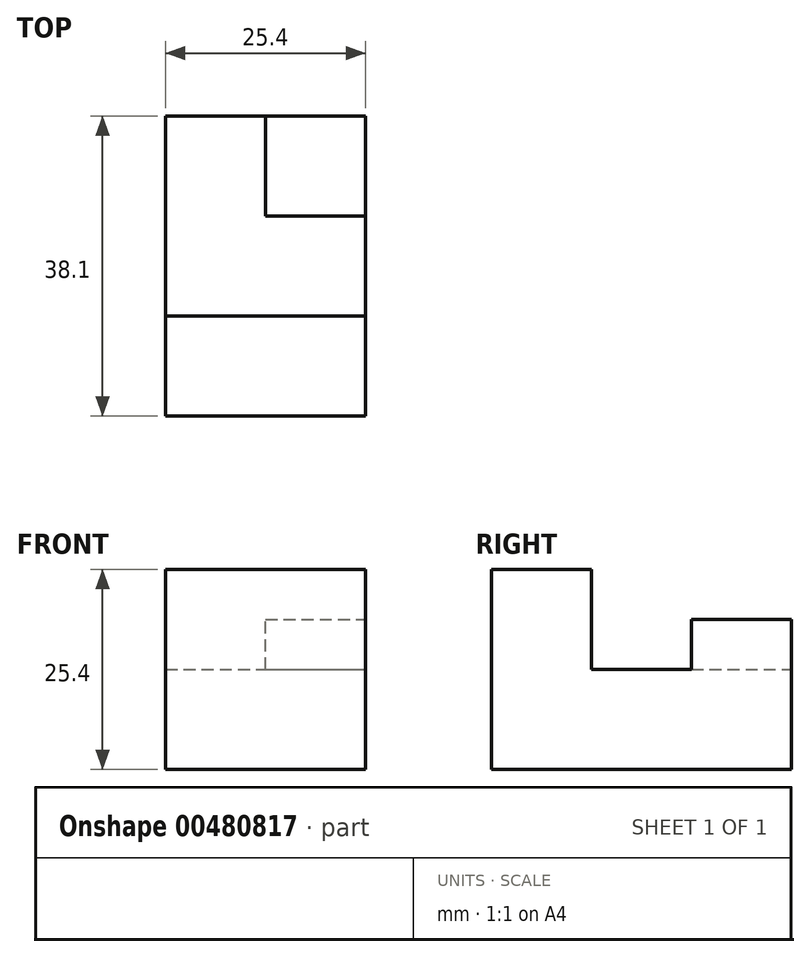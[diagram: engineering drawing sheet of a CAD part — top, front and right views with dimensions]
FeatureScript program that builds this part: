
annotation { "Feature Type Name" : "Feature", "Feature Type Description" : "" }
export const myFeature = defineFeature(function(context is Context, id is Id, definition is map)
    precondition{}
    {
        {
            var Q0;
            Q0=qCreatedBy(makeId("Right.planeOp"),FACE);
            var sketch = newSketch(context, id + "F0", { "sketchPlane" : qUnion([Q0])});
            skLineSegment(sketch, "E0", {"start": v(-38.1, 25.4) * mm, "end": v(-38.1, 0) * mm});
            skLineSegment(sketch, "E1", {"start": v(-38.1, 0) * mm, "end": v(0, 0) * mm});
            skLineSegment(sketch, "E2", {"start": v(0, 0) * mm, "end": v(0, 12.7) * mm});
            skLineSegment(sketch, "E3", {"start": v(0, 12.7) * mm, "end": v(-25.4, 12.7) * mm});
            skLineSegment(sketch, "E4", {"start": v(-25.4, 12.7) * mm, "end": v(-25.4, 25.4) * mm});
            skLineSegment(sketch, "E5", {"start": v(-25.4, 25.4) * mm, "end": v(-38.1, 25.4) * mm});
            skSolve(sketch);
        }
        {
            var Q0;
            Q0=qCreatedBy(makeId("Right.planeOp"),FACE);
            var sketch = newSketch(context, id + "F1", { "sketchPlane" : qUnion([Q0])});
            skLineSegment(sketch, "E6", {"start": v(0, 12.7) * mm, "end": v(0, 19.05) * mm});
            skLineSegment(sketch, "E7", {"start": v(0, 19.05) * mm, "end": v(-12.7, 19.05) * mm});
            skLineSegment(sketch, "E8", {"start": v(-12.7, 19.05) * mm, "end": v(-12.7, 12.7) * mm});
            skLineSegment(sketch, "E9", {"start": v(-12.7, 12.7) * mm, "end": v(0, 12.7) * mm});
            skSolve(sketch);
        }
        {
            var Q0;
            Q0=makeQuery(id+"F0.imprint","IMPRINT",FACE,{"disambiguationData":[TD([[makeQuery(id+"F0.imprint","IMPRINT",EDGE,{"derivedFrom":sQuery(id+"F0.wireOp",EDGE,"E0")}),1.0]])]});
            extrude(context, id + "F2", {"entities" : qUnion([Q0]), "oppositeDirection" : true, "depth" : 25.4 * mm});
        }
        {
            var Q0;
            Q0=makeQuery(id+"F1.imprint","IMPRINT",FACE,{"disambiguationData":[TD([[makeQuery(id+"F1.imprint","IMPRINT",EDGE,{"derivedFrom":sQuery(id+"F1.wireOp",EDGE,"E6")}),1.0]])]});
            extrude(context, id + "F3", {"entities" : qUnion([Q0]), "operationType" : NewBodyOperationType.ADD, "oppositeDirection" : true, "depth" : 12.7 * mm});
        }
    });
